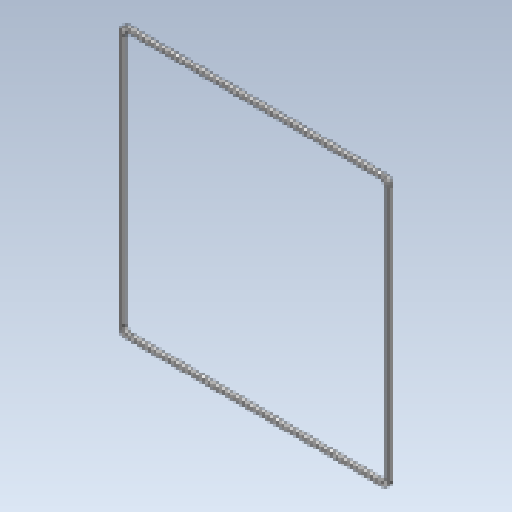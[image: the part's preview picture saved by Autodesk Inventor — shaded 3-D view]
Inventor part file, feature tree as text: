
AUTODESK INVENTOR PART (.ipt)
format: ipt  version: 2023 (Build 270158030, 158C)  size: 106,496 bytes
history: native  units: mm
features: extrude x1, fillet x1, sketch x1
ambient origin geometry x8: Origin, YZ Plane, XZ Plane, XY Plane, X Axis, Y Axis, Z Axis, Center Point
bodies: Solid1 (feature_tree)
feature tree (3):
  extrude  "Extrusion1"  Depth=230.0mm
  fillet  "Fillet1"  Radius=115.0mm
  sketch  "Sketch1"  dims[d0=230.0mm d1=230.0mm d2=115.0mm d3=115.0mm d4=3.0mm d5=3.0mm d6=0.0mm d7=5.0mm]
